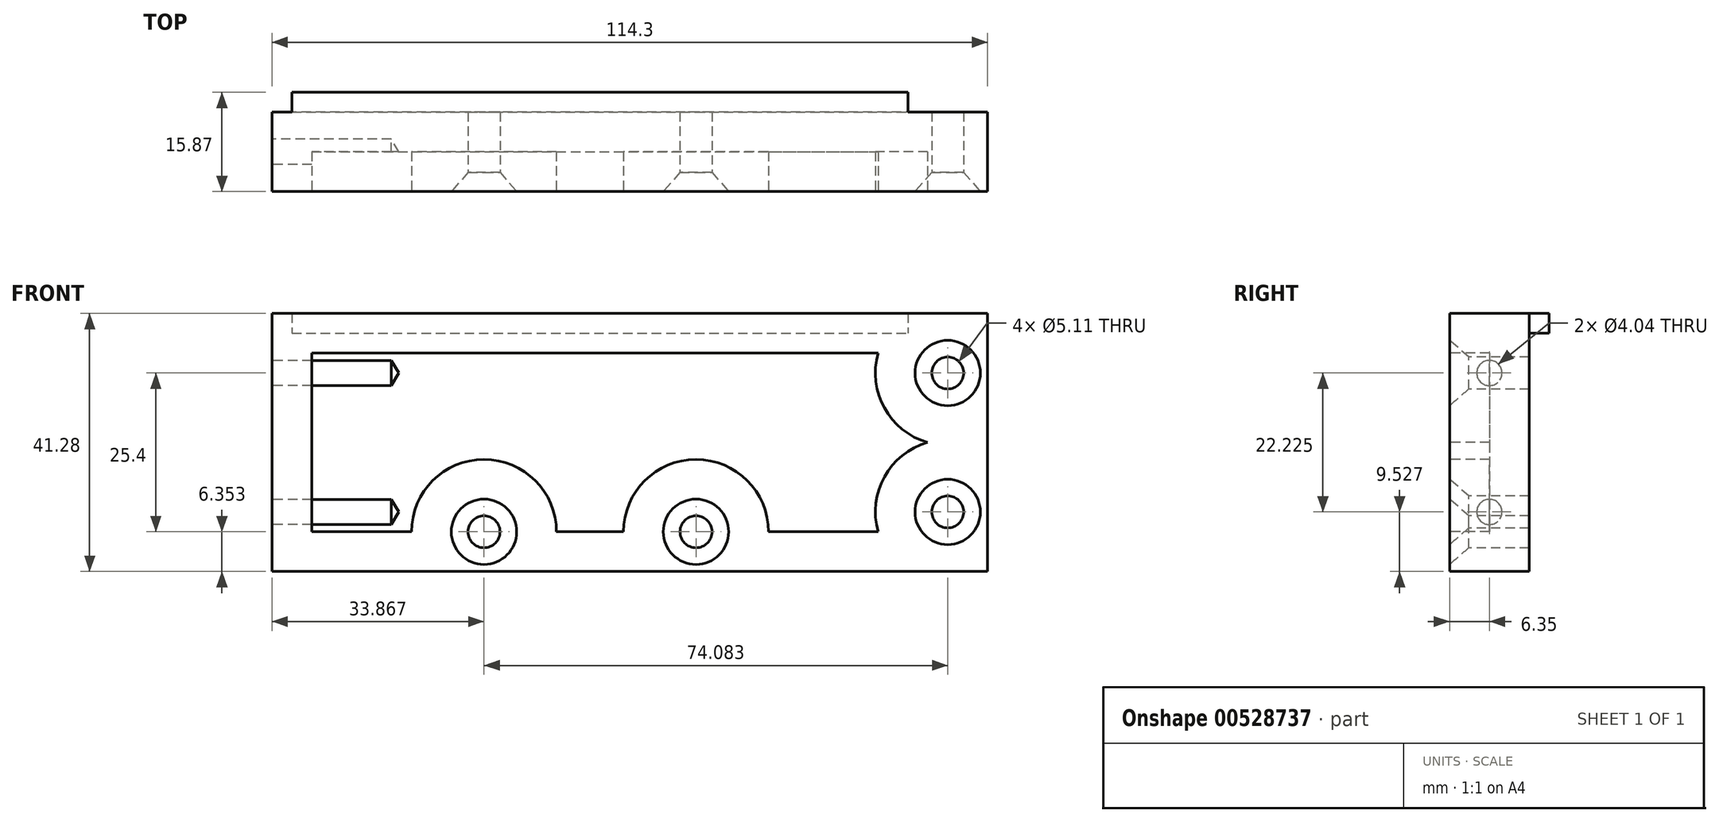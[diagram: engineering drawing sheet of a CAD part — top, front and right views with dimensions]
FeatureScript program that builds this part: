
annotation { "Feature Type Name" : "Feature", "Feature Type Description" : "" }
export const myFeature = defineFeature(function(context is Context, id is Id, definition is map)
    precondition{}
    {
        {
            var Q0;
            Q0=qCreatedBy(makeId("Front.planeOp"),FACE);
            var sketch = newSketch(context, id + "F0", { "sketchPlane" : qUnion([Q0])});
            skLineSegment(sketch, "E0.bottom", {"start": v(57.15, -20.64) * mm, "end": v(-57.15, -20.64) * mm});
            skLineSegment(sketch, "E0.top", {"start": v(57.15, 20.64) * mm, "end": v(-57.15, 20.64) * mm});
            skLineSegment(sketch, "E0.left", {"start": v(57.15, -20.64) * mm, "end": v(57.15, 20.64) * mm});
            skLineSegment(sketch, "E0.right", {"start": v(-57.15, -20.64) * mm, "end": v(-57.15, 20.64) * mm});
            skPoint(sketch, "E0.middle", {"position": v(0, 0) * mm});
            skSolve(sketch);
        }
        {
            var Q0;
            Q0 = qSketchRegion(id + "F0", true);
            extrude(context, id + "F1", {"entities" : qUnion([Q0]), "depth" : 12.7 * mm, "offsetDistance" : 25.4 * mm});
        }
        {
            var Q0;
            Q0=makeQuery(id+"F1.opExtrude","CAP_FACE",FACE,{"disambiguationData":[OSD([sQuery(id+"F0.wireOp",EDGE,"E0.bottom"),sQuery(id+"F0.wireOp",EDGE,"E0.top"),sQuery(id+"F0.wireOp",EDGE,"E0.left"),sQuery(id+"F0.wireOp",EDGE,"E0.right")])],"isStart":false});
            var sketch = newSketch(context, id + "F2", { "sketchPlane" : qUnion([Q0])});
            skLineSegment(sketch, "E1", {"start": v(50.8, 20.64) * mm, "end": v(50.8, -20.64) * mm, "construction": true});
            skPoint(sketch, "E2", {"position": v(50.8, -11.11) * mm});
            skPoint(sketch, "E3", {"position": v(50.8, 11.11) * mm});
            skLineSegment(sketch, "E4", {"start": v(-57.15, -14.29) * mm, "end": v(57.15, -14.29) * mm, "construction": true});
            skLineSegment(sketch, "E5", {"start": v(44.45, 20.64) * mm, "end": v(44.45, -20.64) * mm, "construction": true});
            skLineSegment(sketch, "E6", {"start": v(-57.15, -7.94) * mm, "end": v(57.15, -7.94) * mm, "construction": true});
            skPoint(sketch, "E7", {"position": v(-23.28, -14.29) * mm});
            skPoint(sketch, "E8", {"position": v(10.58, -14.29) * mm});
            skSolve(sketch);
        }
        {
            var Q0;
            Q0=sQuery(id+"F2.wireOp",VERTEX,"E3");
            var Q1;
            Q1=sQuery(id+"F2.wireOp",VERTEX,"E2");
            var Q2;
            Q2=sQuery(id+"F2.wireOp",VERTEX,"E7");
            var Q3;
            Q3=sQuery(id+"F2.wireOp",VERTEX,"E8");
            var Q4;
            Q4=makeQuery(id+"F1.opExtrude","SWEPT_BODY",BODY,{"disambiguationData":[OSD([sQuery(id+"F0.wireOp",EDGE,"E0.bottom"),sQuery(id+"F0.wireOp",EDGE,"E0.top"),sQuery(id+"F0.wireOp",EDGE,"E0.left"),sQuery(id+"F0.wireOp",EDGE,"E0.right")])]});
            hole(context, id + "F3", {"style" : HoleStyle.C_SINK, "endStyle" : HoleEndStyle.THROUGH, "standardTappedOrClearance" : lookupTablePath({ "standard" : "ANSI", "fit" : "Normal (ASME)", "size" : "#10", "type" : "Clearance" }), "standardBlindInLast" : lookupTablePath({ "fit" : "Free", "standard" : "ANSI", "size" : "#10", "type" : "Clearance" }), "holeDiameter" : 5.1 * mm, "cSinkDiameter" : 10.44 * mm, "cSinkAngle" : 82 * degree, "isTappedThrough" : true, "tappedDepth" : 12.7 * mm, "tapClearance" : 3, "locations" : qUnion([Q0, Q1, Q2, Q3]), "scope" : qUnion([Q4])});
        }
        {
            var Q0;
            Q0=makeQuery(id+"F1.opExtrude","SWEPT_FACE",FACE,{"disambiguationData":[OSD([sQuery(id+"F0.wireOp",EDGE,"E0.right")])]});
            var sketch = newSketch(context, id + "F4", { "sketchPlane" : qUnion([Q0])});
            skLineSegment(sketch, "E9", {"start": v(6.35, 20.64) * mm, "end": v(6.35, -20.64) * mm, "construction": true});
            skPoint(sketch, "E10", {"position": v(6.35, 11.11) * mm});
            skPoint(sketch, "E11", {"position": v(6.35, -11.11) * mm});
            skSolve(sketch);
        }
        {
            var Q0;
            Q0=sQuery(id+"F4.wireOp",VERTEX,"E10");
            var Q1;
            Q1=sQuery(id+"F4.wireOp",VERTEX,"E11");
            var Q2;
            Q2=makeQuery(id+"F1.opExtrude","SWEPT_BODY",BODY,{"disambiguationData":[OSD([sQuery(id+"F0.wireOp",EDGE,"E0.bottom"),sQuery(id+"F0.wireOp",EDGE,"E0.top"),sQuery(id+"F0.wireOp",EDGE,"E0.left"),sQuery(id+"F0.wireOp",EDGE,"E0.right")])]});
            hole(context, id + "F5", {"style" : HoleStyle.SIMPLE, "endStyle" : HoleEndStyle.BLIND, "standardTappedOrClearance" : lookupTablePath({ "standard" : "ANSI", "engagement" : "75%", "pitch" : "32 tpi", "size" : "#10", "type" : "Tapped" }), "standardBlindInLast" : lookupTablePath({ "standard" : "ANSI", "engagement" : "75%", "pitch" : "32 tpi", "size" : "#10", "type" : "Tapped" }), "holeDiameter" : 4.04 * mm, "showTappedDepth" : true, "holeDepth" : 19.05 * mm, "isTappedThrough" : true, "tappedDepth" : 16.67 * mm, "tapClearance" : 3, "locations" : qUnion([Q0, Q1]), "scope" : qUnion([Q2]), "majorDiameter" : 4.83 * mm});
        }
        {
            var Q0;
            Q0=makeQuery(id+"F1.opExtrude","CAP_FACE",FACE,{"disambiguationData":[OSD([sQuery(id+"F0.wireOp",EDGE,"E0.bottom"),sQuery(id+"F0.wireOp",EDGE,"E0.top"),sQuery(id+"F0.wireOp",EDGE,"E0.left"),sQuery(id+"F0.wireOp",EDGE,"E0.right")])],"isStart":true});
            var sketch = newSketch(context, id + "F6", { "sketchPlane" : qUnion([Q0])});
            skLineSegment(sketch, "E12.bottom", {"start": v(53.97, 20.64) * mm, "end": v(-44.45, 20.64) * mm});
            skLineSegment(sketch, "E12.top", {"start": v(53.97, 17.46) * mm, "end": v(-44.45, 17.46) * mm});
            skLineSegment(sketch, "E12.left", {"start": v(53.98, 20.64) * mm, "end": v(53.98, 17.46) * mm});
            skLineSegment(sketch, "E12.right", {"start": v(-44.45, 20.64) * mm, "end": v(-44.45, 17.46) * mm});
            skSolve(sketch);
        }
        {
            var Q0;
            Q0 = qSketchRegion(id + "F6", true);
            extrude(context, id + "F7", {"entities" : qUnion([Q0]), "operationType" : NewBodyOperationType.ADD, "depth" : 3.17 * mm, "offsetDistance" : 25.4 * mm});
        }
        {
            var Q0;
            Q0=makeQuery(id+"F1.opExtrude","CAP_FACE",FACE,{"disambiguationData":[OSD([sQuery(id+"F0.wireOp",EDGE,"E0.bottom"),sQuery(id+"F0.wireOp",EDGE,"E0.top"),sQuery(id+"F0.wireOp",EDGE,"E0.left"),sQuery(id+"F0.wireOp",EDGE,"E0.right")])],"isStart":false});
            var sketch = newSketch(context, id + "F8", { "sketchPlane" : qUnion([Q0])});
            skLineSegment(sketch, "E13.bottom", {"start": v(-50.8, 14.29) * mm, "end": v(39.67, 14.29) * mm});
            skLineSegment(sketch, "E13.top", {"start": v(-50.8, -14.29) * mm, "end": v(-34.85, -14.29) * mm});
            skLineSegment(sketch, "E13.left", {"start": v(-50.8, 14.29) * mm, "end": v(-50.8, -14.29) * mm});
            skArc(sketch, "E14", {"start": v(-11.71, -14.29) * mm, "mid": v(-23.28, -2.72) * mm, "end": v(-34.85, -14.29) * mm});
            skArc(sketch, "E15", {"start": v(22.15, -14.29) * mm, "mid": v(10.58, -2.72) * mm, "end": v(-0.99, -14.29) * mm});
            skArc(sketch, "E16", {"start": v(47.58, 0) * mm, "mid": v(40.68, -5.51) * mm, "end": v(39.67, -14.29) * mm});
            skArc(sketch, "E17", {"start": v(39.67, 14.29) * mm, "mid": v(40.68, 5.51) * mm, "end": v(47.58, 0) * mm});
            skLineSegment(sketch, "E18.trimOffspring", {"start": v(-11.71, -14.29) * mm, "end": v(-0.99, -14.29) * mm});
            skLineSegment(sketch, "E19.trimOffspring", {"start": v(22.15, -14.29) * mm, "end": v(39.67, -14.29) * mm});
            skSolve(sketch);
        }
        {
            var Q0;
            Q0 = qSketchRegion(id + "F8", true);
            extrude(context, id + "F9", {"entities" : qUnion([Q0]), "operationType" : NewBodyOperationType.REMOVE, "oppositeDirection" : true, "depth" : 6.35 * mm, "offsetDistance" : 25.4 * mm});
        }
    });
